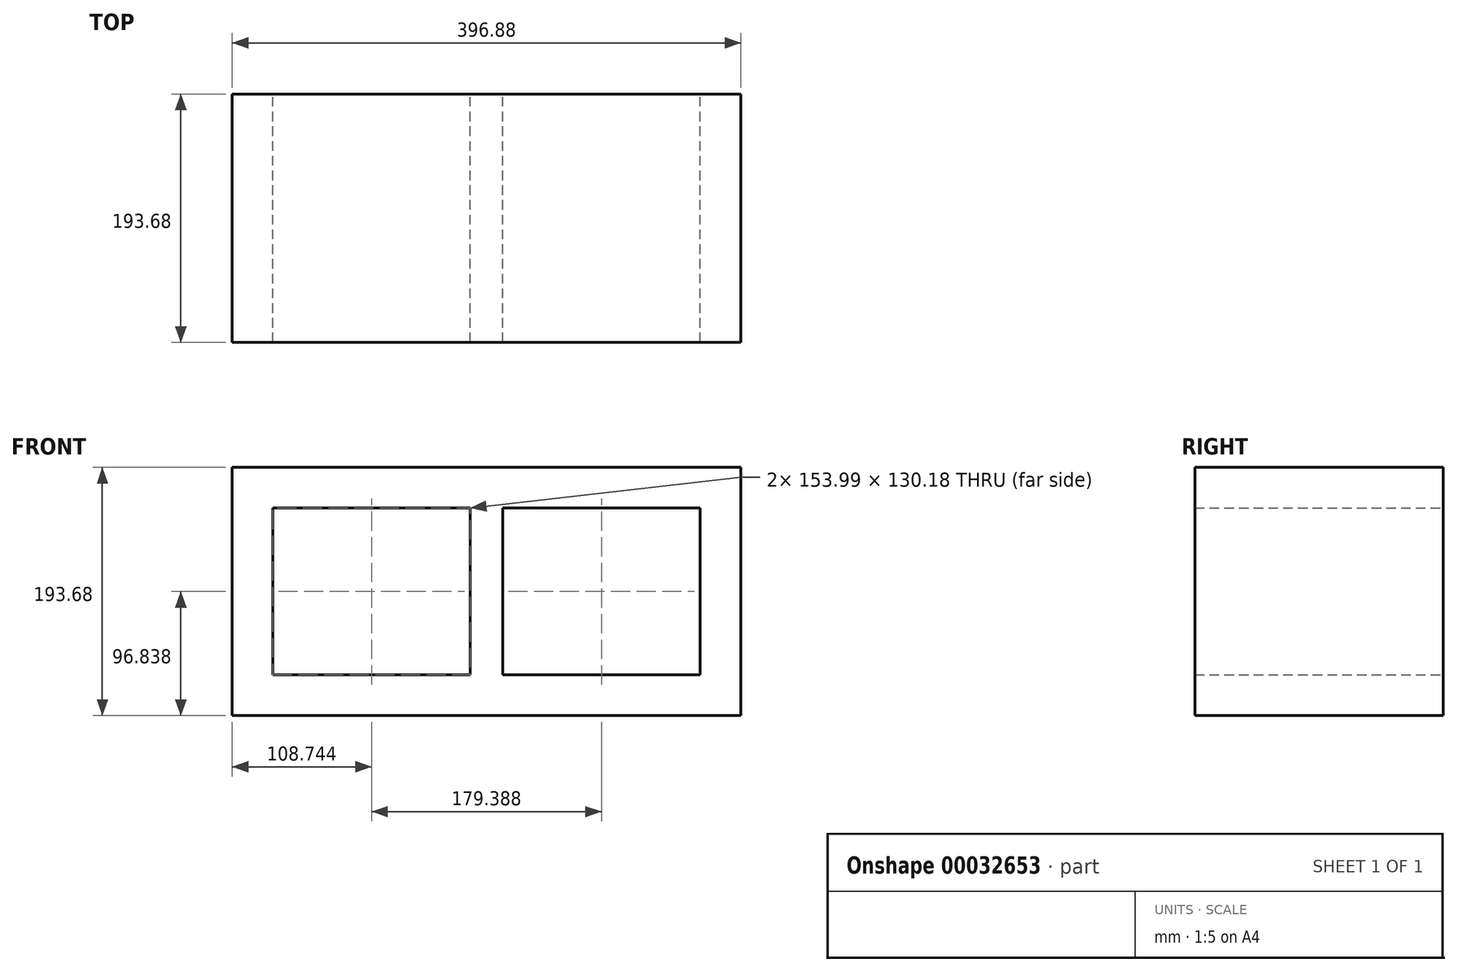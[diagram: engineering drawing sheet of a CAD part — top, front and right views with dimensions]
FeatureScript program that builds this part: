
annotation { "Feature Type Name" : "Feature", "Feature Type Description" : "" }
export const myFeature = defineFeature(function(context is Context, id is Id, definition is map)
    precondition{}
    {
        {
            var Q0;
            Q0=qCreatedBy(makeId("Front.planeOp"),FACE);
            var sketch = newSketch(context, id + "F0", { "sketchPlane" : qUnion([Q0])});
            skLineSegment(sketch, "E0", {"start": v(0, 0) * mm, "end": v(0, 193.67) * mm});
            skLineSegment(sketch, "E1", {"start": v(0, 193.67) * mm, "end": v(396.88, 193.67) * mm});
            skLineSegment(sketch, "E2", {"start": v(396.88, 193.67) * mm, "end": v(396.88, 0) * mm});
            skLineSegment(sketch, "E3", {"start": v(0, 0) * mm, "end": v(396.88, 0) * mm});
            skLineSegment(sketch, "E4.bottom", {"start": v(31.75, 161.93) * mm, "end": v(185.74, 161.93) * mm});
            skLineSegment(sketch, "E4.top", {"start": v(31.75, 31.75) * mm, "end": v(185.74, 31.75) * mm});
            skLineSegment(sketch, "E4.left", {"start": v(31.75, 161.92) * mm, "end": v(31.75, 31.75) * mm});
            skLineSegment(sketch, "E4.right", {"start": v(185.74, 161.93) * mm, "end": v(185.74, 31.75) * mm});
            skLineSegment(sketch, "E5.bottom", {"start": v(211.14, 161.93) * mm, "end": v(365.13, 161.93) * mm});
            skLineSegment(sketch, "E5.top", {"start": v(211.14, 31.75) * mm, "end": v(365.13, 31.75) * mm});
            skLineSegment(sketch, "E5.left", {"start": v(211.14, 161.93) * mm, "end": v(211.14, 31.75) * mm});
            skLineSegment(sketch, "E5.right", {"start": v(365.13, 161.93) * mm, "end": v(365.13, 31.75) * mm});
            skPoint(sketch, "E6", {"position": v(185.74, 96.84) * mm});
            skPoint(sketch, "E7", {"position": v(211.14, 96.84) * mm});
            skPoint(sketch, "E8", {"position": v(288.13, 161.93) * mm});
            skPoint(sketch, "E9", {"position": v(365.13, 96.84) * mm});
            skPoint(sketch, "E10", {"position": v(396.88, 96.84) * mm});
            skPoint(sketch, "E11", {"position": v(288.13, 31.75) * mm});
            skPoint(sketch, "E12", {"position": v(288.13, 0) * mm});
            skSolve(sketch);
        }
        {
            var Q0;
            Q0=qSketchRegion(id+"F0",true);
            extrude(context, id + "F1", {"entities" : qUnion([Q0]), "depth" : 193.67 * mm});
        }
    });
